# Revit family: Поли-Групп_КлапанОбратныйEAZ-KVR_DN50-300
name_source: partatom
category: Арматура трубопроводов
units: mm (PartAtom-declared; Revit-internal decimal feet)

## family parameters
Всегда вертикально = Да
На основе рабочей плоскости = Нет
Общий = Нет
При загрузке вырезать с полостями = Нет
Размер круглого соединителя = Использовать диаметр
Тип детали = Нормальный

## types (18) — shared parameters
ADSK_URL страницы изделия = https://www.polycorr.ru
ADSK_Версия Revit = 2019
ADSK_Единица измерения = шт.
ADSK_Завод-изготовитель = ООО ПК «Поли-Групп»
ADSK_Количество = 1
ADSK_Материал = Высокопрочный чугун GGG-40
ADSK_Материал наименование = Высокопрочный чугун с шаровидным графитом (GGG-40)
f = 3 мм
Класс герметичности = А по ГОСТ Р 9544-2015
Материал уплотнителя = NBR
Материал шара = Алюминий
Назначение = Для предотвращения обратного потока среды на трубопроводах
Покрытие = Высококачественное эпоксидное покрытие толщиной 300 мкм.
Рабочая среда = Питьевая вода, техническая вода, канализационные стоки, морская вода.
Разработчик = https://3dbim.pro
ТВ = КлапанОбратныйEAZ-KVR_DN50-300_Поли-Групп
Температура рабочей среды = 0 до +70°С
Тип присоединения = Фланцевое
Угол = 45.00°
Угол2 = 90.00°

## per-type parameters (varying)
| type | ADSK_Марка | ADSK_Масса | ADSK_Масса_Текст | ADSK_Наименование | ADSK_Наименование краткое | D | D1 | D2 | DN | D_нар | H | Kv | L | PN | b | b1 | d1 | h | h2 | l | r | r2 |
| 50-10 | EAZ-DCh-4 DN50 PN10 | 8 | 8 | Клапан обратный EAZ KVR шаровой фланцевый DN50 PN10 | Клапан обратный EAZ KVR DN50 PN10 | 165 мм | 125 мм | 102 мм | 50 мм | 90 мм | 116 мм | 0.5 м³/ч | 200 мм | 10.0 бары | 19 мм | 10 мм | 5 мм | 23 мм | 23 мм | 114 мм | 38 мм | 43 мм |
| 65-10 | EAZ-DCh-4 DN65 PN10 | 12 | 12 | Клапан обратный EAZ KVR шаровой фланцевый DN65 PN10 | Клапан обратный EAZ KVR DN65 PN10 | 185 мм | 145 мм | 122 мм | 65 мм | 105 мм | 151 мм | 0.5 м³/ч | 240 мм | 10.0 бары | 19 мм | 10 мм | 7 мм | 30 мм | 30 мм | 152 мм | 44 мм | 51 мм |
| 80-10 | EAZ-DCh-4 DN80 PN10 | 14.3 | 14.3 | Клапан обратный EAZ KVR шаровой фланцевый DN80 PN10 | Клапан обратный EAZ KVR DN80 PN10 | 200 мм | 160 мм | 138 мм | 80 мм | 120 мм | 169 мм | 0.5 м³/ч | 260 мм | 10.0 бары | 19 мм | 10 мм | 8 мм | 34 мм | 34 мм | 170 мм | 50 мм | 58 мм |
| 100-10 | EAZ-DCh-4 DN100 PN10 | 20 | 20 | Клапан обратный EAZ KVR шаровой фланцевый DN100 PN10 | Клапан обратный EAZ KVR DN100 PN10 | 220 мм | 180 мм | 158 мм | 100 мм | 140 мм | 196 мм | 0.5 м³/ч | 300 мм | 10.0 бары | 19 мм | 10 мм | 10 мм | 39 мм | 39 мм | 196 мм | 59 мм | 68 мм |
| 125-10 | EAZ-DCh-4 DN125 PN10 | 28.1 | 28.1 | Клапан обратный EAZ KVR шаровой фланцевый DN125 PN10 | Клапан обратный EAZ KVR DN125 PN10 | 250 мм | 210 мм | 188 мм | 125 мм | 165 мм | 228 мм | 0.5 м³/ч | 350 мм | 10.0 бары | 19 мм | 10 мм | 13 мм | 46 мм | 46 мм | 228 мм | 69 мм | 80 мм |
| 150-10 | EAZ-DCh-4 DN150 PN10 | 36 | 36 | Клапан обратный EAZ KVR шаровой фланцевый DN150 PN10 | Клапан обратный EAZ KVR DN150 PN10 | 285 мм | 240 мм | 212 мм | 150 мм | 190 мм | 262 мм | 1.2 м³/ч | 400 мм | 10.0 бары | 19 мм | 10 мм | 15 мм | 52 мм | 52 мм | 262 мм | 80 мм | 92 мм |
| 200-10 | EAZ-DCh-4 DN200 PN10 | 64 | 64 | Клапан обратный EAZ KVR шаровой фланцевый DN200 PN10 | Клапан обратный EAZ KVR DN200 PN10 | 340 мм | 295 мм | 268 мм | 200 мм | 240 мм | 354 мм | 1.2 м³/ч | 500 мм | 10.0 бары | 24 мм | 12 мм | 20 мм | 71 мм | 71 мм | 359 мм | 101 мм | 116 мм |
| 250-10 | EAZ-DCh-4 DN250 PN10 | 140 | 140 | Клапан обратный EAZ KVR шаровой фланцевый DN250 PN10 | Клапан обратный EAZ KVR DN250 PN10 | 395 мм | 350 мм | 320 мм | 250 мм | 290 мм | 460 мм | 1.2 м³/ч | 600 мм | 10.0 бары | 24 мм | 12 мм | 25 мм | 92 мм | 92 мм | 472 мм | 122 мм | 140 мм |
| 300-10 | EAZ-DCh-4 DN300 PN10 | 195 | 195 | Клапан обратный EAZ KVR шаровой фланцевый DN300 PN10 | Клапан обратный EAZ KVR DN300 PN10 | 445 мм | 400 мм | 370 мм | 300 мм | 340 мм | 528 мм | 1.2 м³/ч | 700 мм | 10.0 бары | 26 мм | 13 мм | 30 мм | 106 мм | 106 мм | 540 мм | 143 мм | 164 мм |
| 50-16 | EAZ-DCh-4 DN50 PN16 | 8 | 8 | Клапан обратный EAZ KVR шаровой фланцевый DN50 PN16 | Клапан обратный EAZ KVR DN50 PN16 | 125 мм | 125 мм | 102 мм | 50 мм | 90 мм | 116 мм | 0.5 м³/ч | 200 мм | 16.0 бары | 19 мм | 10 мм | 5 мм | 23 мм | 23 мм | 114 мм | 38 мм | 43 мм |
| 65-16 | EAZ-DCh-4 DN65 PN16 | 12 | 12 | Клапан обратный EAZ KVR шаровой фланцевый DN65 PN16 | Клапан обратный EAZ KVR DN65 PN16 | 145 мм | 145 мм | 122 мм | 65 мм | 105 мм | 151 мм | 0.5 м³/ч | 240 мм | 16.0 бары | 19 мм | 10 мм | 7 мм | 30 мм | 30 мм | 152 мм | 44 мм | 51 мм |
| 80-16 | EAZ-DCh-4 DN80 PN16 | 14.3 | 14.3 | Клапан обратный EAZ KVR шаровой фланцевый DN80 PN16 | Клапан обратный EAZ KVR DN80 PN16 | 160 мм | 160 мм | 138 мм | 80 мм | 120 мм | 169 мм | 0.5 м³/ч | 260 мм | 16.0 бары | 19 мм | 10 мм | 8 мм | 34 мм | 34 мм | 170 мм | 50 мм | 58 мм |
| 100-16 | EAZ-DCh-4 DN100 PN16 | 20 | 20 | Клапан обратный EAZ KVR шаровой фланцевый DN100 PN16 | Клапан обратный EAZ KVR DN100 PN16 | 180 мм | 180 мм | 158 мм | 100 мм | 140 мм | 196 мм | 0.5 м³/ч | 300 мм | 16.0 бары | 19 мм | 10 мм | 10 мм | 39 мм | 39 мм | 196 мм | 59 мм | 68 мм |
| 125-16 | EAZ-DCh-4 DN125 PN16 | 28.1 | 28.1 | Клапан обратный EAZ KVR шаровой фланцевый DN125 PN16 | Клапан обратный EAZ KVR DN125 PN16 | 210 мм | 210 мм | 188 мм | 125 мм | 165 мм | 228 мм | 0.5 м³/ч | 350 мм | 16.0 бары | 19 мм | 10 мм | 13 мм | 46 мм | 46 мм | 228 мм | 69 мм | 80 мм |
| 150-16 | EAZ-DCh-4 DN150 PN16 | 36 | 36 | Клапан обратный EAZ KVR шаровой фланцевый DN150 PN16 | Клапан обратный EAZ KVR DN150 PN16 | 240 мм | 240 мм | 212 мм | 150 мм | 190 мм | 262 мм | 1.2 м³/ч | 400 мм | 16.0 бары | 19 мм | 10 мм | 15 мм | 52 мм | 52 мм | 262 мм | 80 мм | 92 мм |
| 200-16 | EAZ-DCh-4 DN200 PN16 | 64 | 64 | Клапан обратный EAZ KVR шаровой фланцевый DN200 PN16 | Клапан обратный EAZ KVR DN200 PN16 | 295 мм | 295 мм | 268 мм | 200 мм | 240 мм | 354 мм | 1.2 м³/ч | 500 мм | 16.0 бары | 24 мм | 12 мм | 20 мм | 71 мм | 71 мм | 359 мм | 101 мм | 116 мм |
| 250-16 | EAZ-DCh-4 DN250 PN16 | 140 | 140 | Клапан обратный EAZ KVR шаровой фланцевый DN250 PN16 | Клапан обратный EAZ KVR DN250 PN16 | 405 мм | 355 мм | 320 мм | 250 мм | 290 мм | 460 мм | 1.2 м³/ч | 600 мм | 16.0 бары | 24 мм | 12 мм | 25 мм | 92 мм | 92 мм | 472 мм | 122 мм | 140 мм |
| 300-16 | EAZ-DCh-4 DN300 PN16 | 195 | 195 | Клапан обратный EAZ KVR шаровой фланцевый DN300 PN16 | Клапан обратный EAZ KVR DN300 PN16 | 460 мм | 410 мм | 378 мм | 300 мм | 340 мм | 528 мм | 1.2 м³/ч | 700 мм | 16.0 бары | 26 мм | 13 мм | 30 мм | 106 мм | 106 мм | 540 мм | 143 мм | 164 мм |
